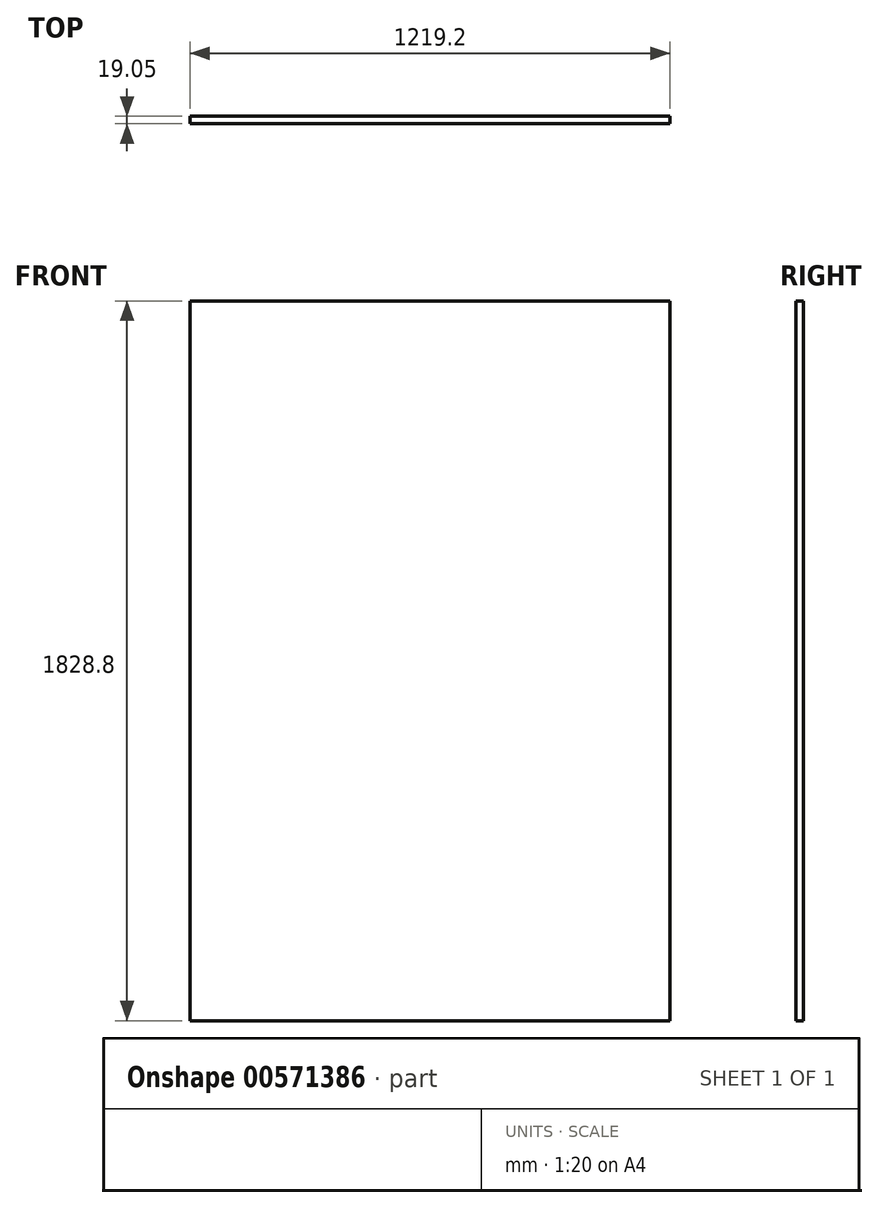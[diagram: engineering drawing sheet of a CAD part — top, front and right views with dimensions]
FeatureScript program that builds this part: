
annotation { "Feature Type Name" : "Feature", "Feature Type Description" : "" }
export const myFeature = defineFeature(function(context is Context, id is Id, definition is map)
    precondition{}
    {
        {
            var Q0;
            Q0=qCreatedBy(makeId("Front.planeOp"),FACE);
            var sketch = newSketch(context, id + "F0", { "sketchPlane" : qUnion([Q0])});
            skLineSegment(sketch, "E0.bottom", {"start": v(-984.25, 1828.8) * mm, "end": v(234.95, 1828.8) * mm});
            skLineSegment(sketch, "E0.top", {"start": v(-984.25, 0) * mm, "end": v(234.95, 0) * mm});
            skLineSegment(sketch, "E0.left", {"start": v(-984.25, 1828.8) * mm, "end": v(-984.25, 0) * mm});
            skLineSegment(sketch, "E0.right", {"start": v(234.95, 1828.8) * mm, "end": v(234.95, 0) * mm});
            skSolve(sketch);
        }
        {
            var Q0;
            Q0=makeQuery(id+"F0.imprint","IMPRINT",FACE,{"disambiguationData":[TD([[makeQuery(id+"F0.imprint","IMPRINT",EDGE,{"derivedFrom":sQuery(id+"F0.wireOp",EDGE,"E0.bottom")}),-1.0]])]});
            extrude(context, id + "F1", {"entities" : qUnion([Q0]), "depth" : 19.05 * mm, "offsetDistance" : 25.4 * mm});
        }
    });
